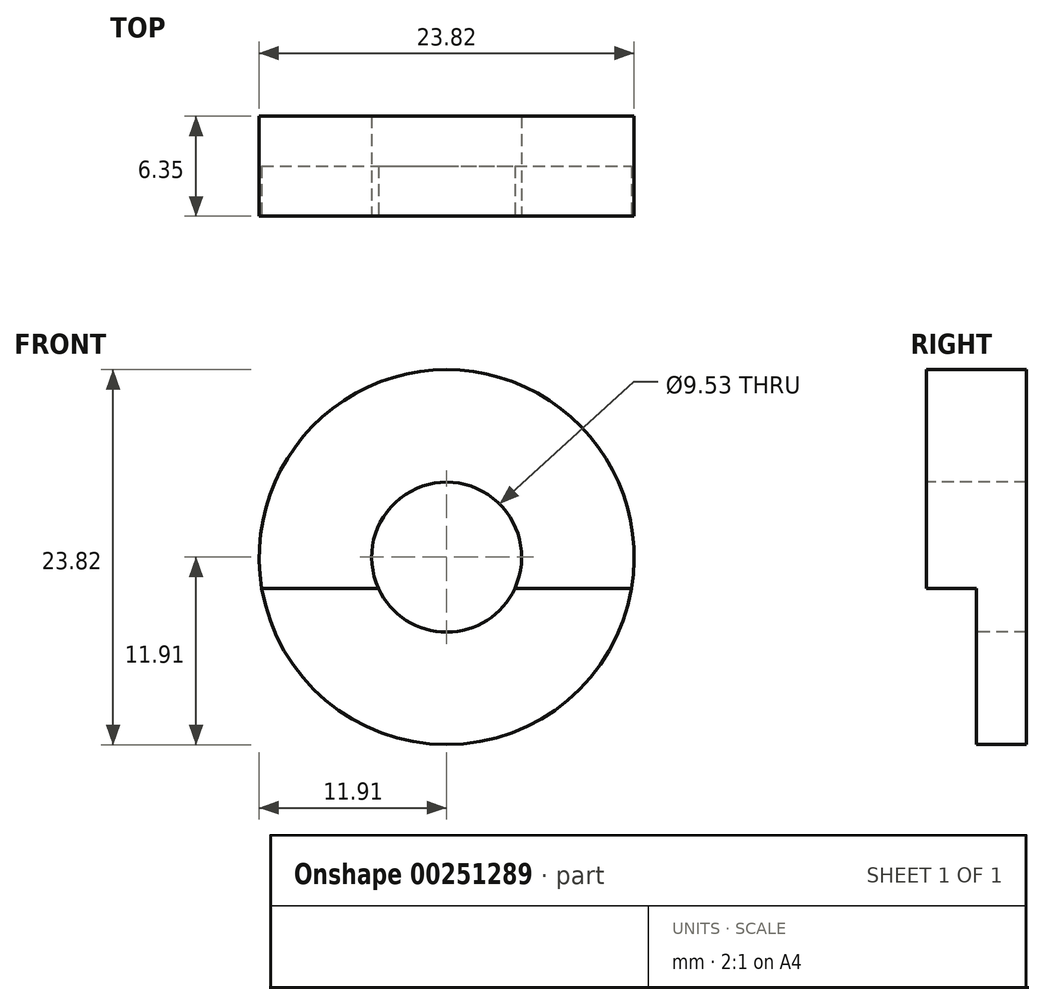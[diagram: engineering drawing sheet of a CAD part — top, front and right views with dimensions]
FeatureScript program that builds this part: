
annotation { "Feature Type Name" : "Feature", "Feature Type Description" : "" }
export const myFeature = defineFeature(function(context is Context, id is Id, definition is map)
    precondition{}
    {
        {
            var Q0;
            Q0=qCreatedBy(makeId("Front.planeOp"),FACE);
            var sketch = newSketch(context, id + "F0", { "sketchPlane" : qUnion([Q0])});
            skCircle(sketch, "E0", {"center": v(0, 0) * mm, "radius": 11.9 * mm});
            skSolve(sketch);
        }
        {
            var Q0;
            Q0 = qSketchRegion(id + "F0", true);
            extrude(context, id + "F1", {"entities" : qUnion([Q0]), "depth" : 6.35 * mm});
        }
        {
            var Q0;
            Q0=makeQuery(id+"F1.opExtrude","CAP_FACE",FACE,{"disambiguationData":[OSD([sQuery(id+"F0.wireOp",EDGE,"E0")])],"isStart":false});
            var sketch = newSketch(context, id + "F2", { "sketchPlane" : qUnion([Q0])});
            skCircle(sketch, "E1", {"center": v(0, 0) * mm, "radius": 4.76 * mm});
            skSolve(sketch);
        }
        {
            var Q0;
            Q0 = qSketchRegion(id + "F2", true);
            extrude(context, id + "F3", {"entities" : qUnion([Q0]), "operationType" : NewBodyOperationType.REMOVE, "oppositeDirection" : true, "depth" : 25.4 * mm});
        }
        {
            var Q0;
            Q0=makeQuery(id+"F1.opExtrude","CAP_FACE",FACE,{"disambiguationData":[OSD([sQuery(id+"F0.wireOp",EDGE,"E0")])],"isStart":false});
            var sketch = newSketch(context, id + "F4", { "sketchPlane" : qUnion([Q0])});
            skLineSegment(sketch, "E2", {"start": v(-16.23, -1.98) * mm, "end": v(17.4, -1.98) * mm});
            skArc(sketch, "E3", {"start": v(-4.33, -1.98) * mm, "mid": v(0, -4.76) * mm, "end": v(4.33, -1.98) * mm});
            skArc(sketch, "E4", {"start": v(-11.74, -1.98) * mm, "mid": v(0, -11.9) * mm, "end": v(11.74, -1.98) * mm});
            skSolve(sketch);
        }
        {
            var Q0;
            Q0 = qSketchRegion(id + "F4", true);
            extrude(context, id + "F5", {"entities" : qUnion([Q0]), "operationType" : NewBodyOperationType.REMOVE, "oppositeDirection" : true, "depth" : 3.17 * mm});
        }
    });
